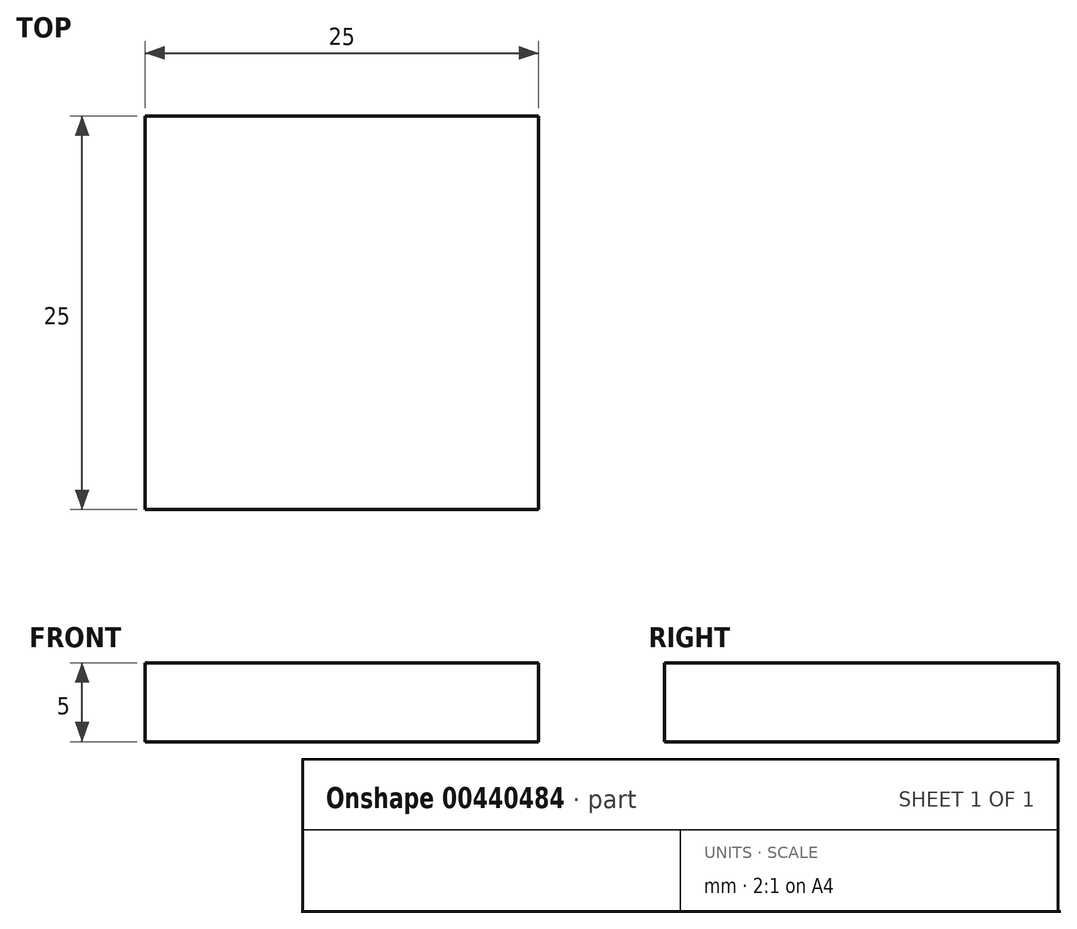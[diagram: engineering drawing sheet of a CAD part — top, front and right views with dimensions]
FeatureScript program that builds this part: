
annotation { "Feature Type Name" : "Feature", "Feature Type Description" : "" }
export const myFeature = defineFeature(function(context is Context, id is Id, definition is map)
    precondition{}
    {
        {
            var Q0;
            Q0=qCreatedBy(makeId("Top.planeOp"),FACE);
            var sketch = newSketch(context, id + "F0", { "sketchPlane" : qUnion([Q0])});
            skLineSegment(sketch, "E0.bottom", {"start": v(-12.5, 12.5) * mm, "end": v(12.5, 12.5) * mm});
            skLineSegment(sketch, "E0.top", {"start": v(-12.5, -12.5) * mm, "end": v(12.5, -12.5) * mm});
            skLineSegment(sketch, "E0.left", {"start": v(-12.5, 12.5) * mm, "end": v(-12.5, -12.5) * mm});
            skLineSegment(sketch, "E0.right", {"start": v(12.5, 12.5) * mm, "end": v(12.5, -12.5) * mm});
            skPoint(sketch, "E0.middle", {"position": v(0, 0) * mm});
            skSolve(sketch);
        }
        {
            var Q0;
            Q0 = qSketchRegion(id + "F0", true);
            extrude(context, id + "F1", {"entities" : qUnion([Q0]), "depth" : 5 * mm, "offsetDistance" : 25 * mm});
        }
    });
